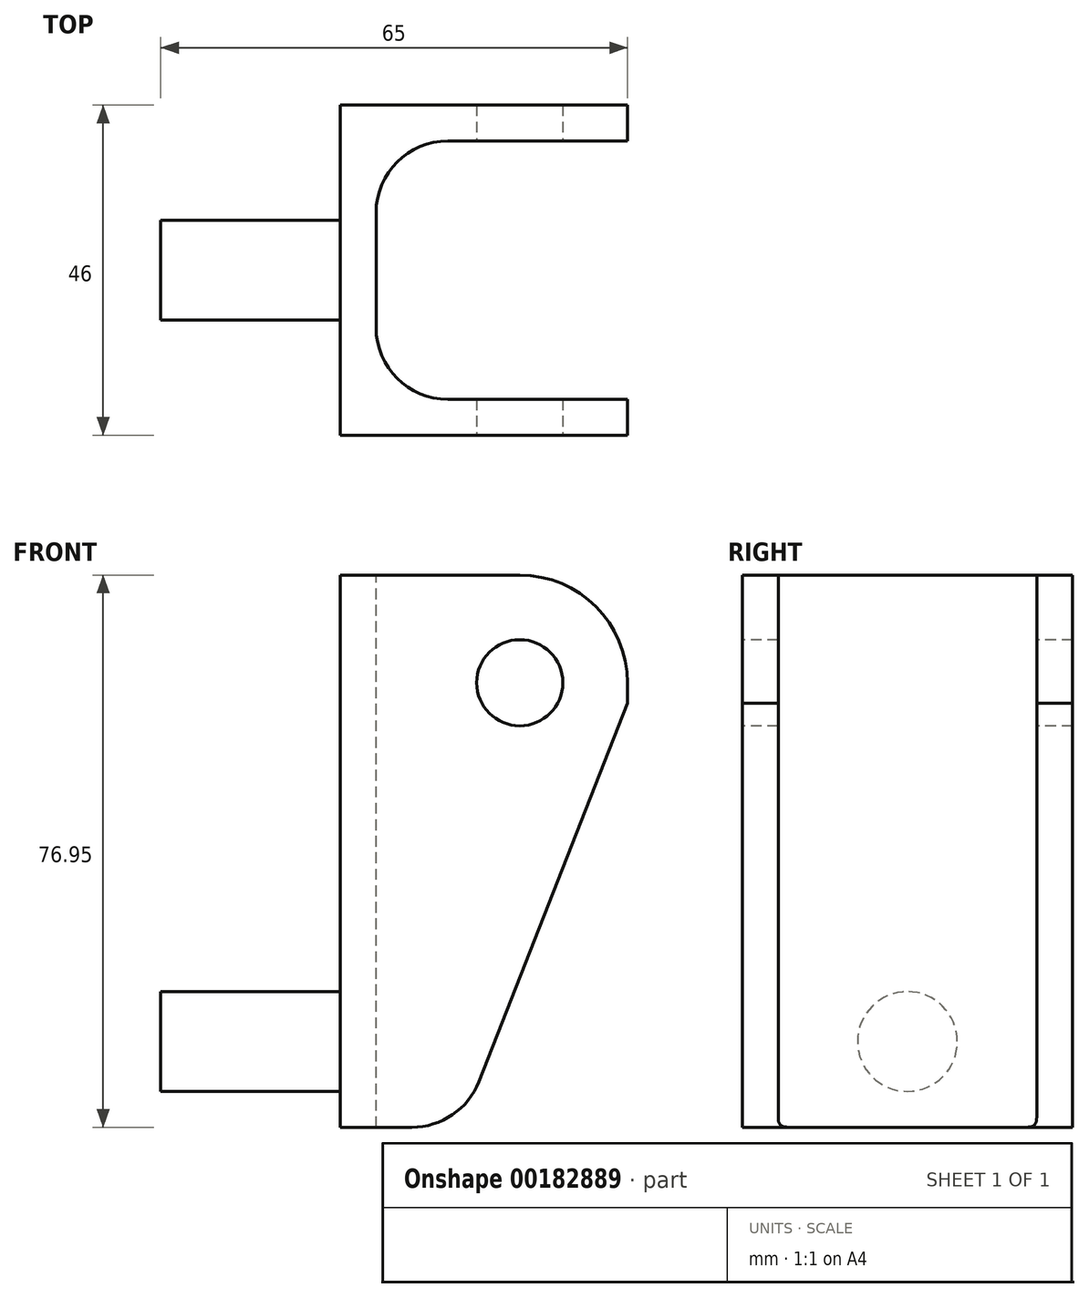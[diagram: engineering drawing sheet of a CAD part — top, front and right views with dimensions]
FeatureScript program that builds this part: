
annotation { "Feature Type Name" : "Feature", "Feature Type Description" : "" }
export const myFeature = defineFeature(function(context is Context, id is Id, definition is map)
    precondition{}
    {
        {
            var Q0;
            Q0=qCreatedBy(makeId("Right.planeOp"),FACE);
            var sketch = newSketch(context, id + "F0", { "sketchPlane" : qUnion([Q0])});
            skCircle(sketch, "E0", {"center": v(0, 0) * mm, "radius": 6.95 * mm});
            skSolve(sketch);
        }
        {
            var Q0;
            Q0 = qSketchRegion(id + "F0", true);
            extrude(context, id + "F1", {"entities" : qUnion([Q0]), "oppositeDirection" : true, "depth" : 25 * mm});
        }
        {
            var Q0;
            Q0=qCreatedBy(makeId("Right.planeOp"),FACE);
            var sketch = newSketch(context, id + "F2", { "sketchPlane" : qUnion([Q0])});
            skLineSegment(sketch, "E1.bottom", {"start": v(23, -11.95) * mm, "end": v(-23, -11.95) * mm});
            skLineSegment(sketch, "E1.top", {"start": v(23, 65) * mm, "end": v(-23, 65) * mm});
            skLineSegment(sketch, "E1.left", {"start": v(23, -11.95) * mm, "end": v(23, 65) * mm});
            skLineSegment(sketch, "E1.right", {"start": v(-23, -11.95) * mm, "end": v(-23, 65) * mm});
            skPoint(sketch, "E1.middle", {"position": v(0, 26.52) * mm});
            skCircle(sketch, "E2.0", {"center": v(0, 0) * mm, "radius": 6.95 * mm});
            skLineSegment(sketch, "E3", {"start": v(-53.36, 50) * mm, "end": v(61.79, 50) * mm, "construction": true});
            skSolve(sketch);
        }
        {
            var Q0;
            Q0 = qSketchRegion(id + "F2", true);
            var Q1;
            Q1=makeQuery(id+"F2.imprint","IMPRINT",FACE,{"disambiguationData":[TD([[makeQuery(id+"F2.imprint","IMPRINT",EDGE,{"derivedFrom":sQuery(id+"F2.wireOp",EDGE,"E2.0")}),1.0]])]});
            extrude(context, id + "F3", {"entities" : qUnion([Q0, Q1]), "operationType" : NewBodyOperationType.ADD, "depth" : 40 * mm});
        }
        {
            var Q0;
            Q0=makeQuery(id+"F3.opExtrude","SWEPT_FACE",FACE,{"disambiguationData":[OSD([sQuery(id+"F2.wireOp",EDGE,"E1.top")])]});
            var sketch = newSketch(context, id + "F4", { "sketchPlane" : qUnion([Q0])});
            skLineSegment(sketch, "E4.0", {"start": v(0, 23) * mm, "end": v(0, -23) * mm});
            skLineSegment(sketch, "E5.0", {"start": v(40, -23) * mm, "end": v(0, -23) * mm});
            skLineSegment(sketch, "E6.0", {"start": v(40, 23) * mm, "end": v(0, 23) * mm});
            skLineSegment(sketch, "E7.0", {"start": v(40, 23) * mm, "end": v(40, -23) * mm});
            skLineSegment(sketch, "E8", {"start": v(40, 18) * mm, "end": v(15, 18) * mm});
            skLineSegment(sketch, "E9", {"start": v(5, 8) * mm, "end": v(5, -8) * mm});
            skLineSegment(sketch, "E10", {"start": v(15, -18) * mm, "end": v(40, -18) * mm});
            skPoint(sketch, "E11.visualSharp", {"position": v(5, 18) * mm});
            skArc(sketch, "E11.filletArc", {"start": v(15, 18) * mm, "mid": v(7.93, 15.07) * mm, "end": v(5, 8) * mm});
            skPoint(sketch, "E12.visualSharp", {"position": v(5, -18) * mm});
            skArc(sketch, "E12.filletArc", {"start": v(5, -8) * mm, "mid": v(7.93, -15.07) * mm, "end": v(15, -18) * mm});
            skSolve(sketch);
        }
        {
            var Q0;
            {var subQ1=sQuery(id+"F4.wireOp",EDGE,"E8");Q0=makeQuery(id+"F4.imprint","IMPRINT",FACE,{"disambiguationData":[TD([[makeQuery(id+"F4.imprint","IMPRINT",EDGE,{"derivedFrom":subQ1}),1.0]])]});}
            extrude(context, id + "F5", {"entities" : qUnion([Q0]), "operationType" : NewBodyOperationType.REMOVE, "endBound" : BoundingType.THROUGH_ALL, "oppositeDirection" : true, "depth" : 25 * mm});
        }
        {
            var Q0;
            Q0=makeQuery(id+"F3.opExtrude","SWEPT_FACE",FACE,{"disambiguationData":[OSD([sQuery(id+"F2.wireOp",EDGE,"E1.right")])]});
            var sketch = newSketch(context, id + "F6", { "sketchPlane" : qUnion([Q0])});
            skLineSegment(sketch, "E13.0", {"start": v(40, 65) * mm, "end": v(0, 65) * mm});
            skLineSegment(sketch, "E14.0", {"start": v(40, -11.95) * mm, "end": v(40, 65) * mm});
            skArc(sketch, "E15", {"start": v(38.96, 44.52) * mm, "mid": v(37.4, 58.45) * mm, "end": v(25, 65) * mm});
            skCircle(sketch, "E16", {"center": v(25, 50) * mm, "radius": 6 * mm});
            skLineSegment(sketch, "E17.0", {"start": v(40, -11.95) * mm, "end": v(0, -11.95) * mm});
            skLineSegment(sketch, "E18.0", {"start": v(0, -11.95) * mm, "end": v(0, 65) * mm});
            skArc(sketch, "E19", {"start": v(10, -11.95) * mm, "mid": v(15.63, -10.21) * mm, "end": v(19.3, -5.6) * mm});
            skLineSegment(sketch, "E20", {"start": v(40, 47.16) * mm, "end": v(19.3, -5.6) * mm});
            skSolve(sketch);
        }
        {
            var Q0;
            {var subQ0=sQuery(id+"F6.wireOp",EDGE,"E14.0");var subQ1=sQuery(id+"F6.wireOp",EDGE,"E13.0");var subQ2=makeQuery(id+"F6.imprint","INTERSECT",VERTEX,{"derivedFrom":[subQ1,subQ0]});Q0=makeQuery(id+"F6.imprint","IMPRINT",FACE,{"disambiguationData":[TD([[makeQuery(id+"F6.imprint","IMPRINT",EDGE,{"disambiguationData":[TD([[subQ2,-1.0]])],"derivedFrom":subQ1}),1.0]])]});}
            var Q1;
            {var subQ4=sQuery(id+"F6.wireOp",EDGE,"E19");Q1=makeQuery(id+"F6.imprint","IMPRINT",FACE,{"disambiguationData":[TD([[makeQuery(id+"F6.imprint","IMPRINT",EDGE,{"derivedFrom":subQ4}),-1.0]])]});}
            var Q2;
            Q2=makeQuery(id+"F6.imprint","IMPRINT",FACE,{"disambiguationData":[TD([[makeQuery(id+"F6.imprint","IMPRINT",EDGE,{"derivedFrom":sQuery(id+"F6.wireOp",EDGE,"E16")}),1.0]])]});
            extrude(context, id + "F7", {"entities" : qUnion([Q0, Q1, Q2]), "operationType" : NewBodyOperationType.REMOVE, "endBound" : BoundingType.THROUGH_ALL, "oppositeDirection" : true, "depth" : 25 * mm});
        }
    });
